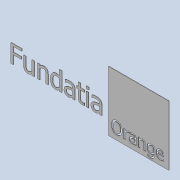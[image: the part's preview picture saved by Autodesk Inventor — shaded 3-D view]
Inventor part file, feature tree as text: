
AUTODESK INVENTOR PART (.ipt)
format: ipt  version: 2020 (Build 240168000, 168)  size: 500,224 bytes
history: native  units: mm
features: extrude x2, sketch x2
ambient origin geometry x8: Origin, YZ Plane, XZ Plane, XY Plane, X Axis, Y Axis, Z Axis, Center Point
bodies: Solid1 (feature_tree)
feature tree (4):
  extrude  "Extrusion1"  Depth=420.0mm
  extrude  "Extrusion2"  Depth=100.0mm
  sketch  "Sketch1"  dims[d0=297.0mm d1=420.0mm]
  sketch  "Sketch2"  dims[d2=0.8mm d3=0.0mm d7=100.0mm d8=100.0mm d9=0.0mm d10=0.0mm]
